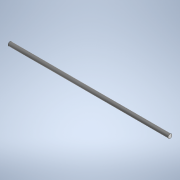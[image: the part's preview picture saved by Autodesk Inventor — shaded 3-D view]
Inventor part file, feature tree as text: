
AUTODESK INVENTOR PART (.ipt)
format: ipt  version: 2021 (Build 250183000, 183)  size: 101,376 bytes
history: native  units: in
note: dims shown in document units (in); Inventor stores cm internally (conversion verified against a paired STEP export)
features: extrude x1, sketch x1
ambient origin geometry x8: Origin, YZ Plane, XZ Plane, XY Plane, X Axis, Y Axis, Z Axis, Center Point
bodies: Solid1 (feature_tree)
feature tree (2):
  extrude  "Extrusion1"  Depth=0.203in TaperAngle=0.0deg
  sketch  "Sketch1"  dims[d0=0.005in d1=0.203in d2=0.0in]
